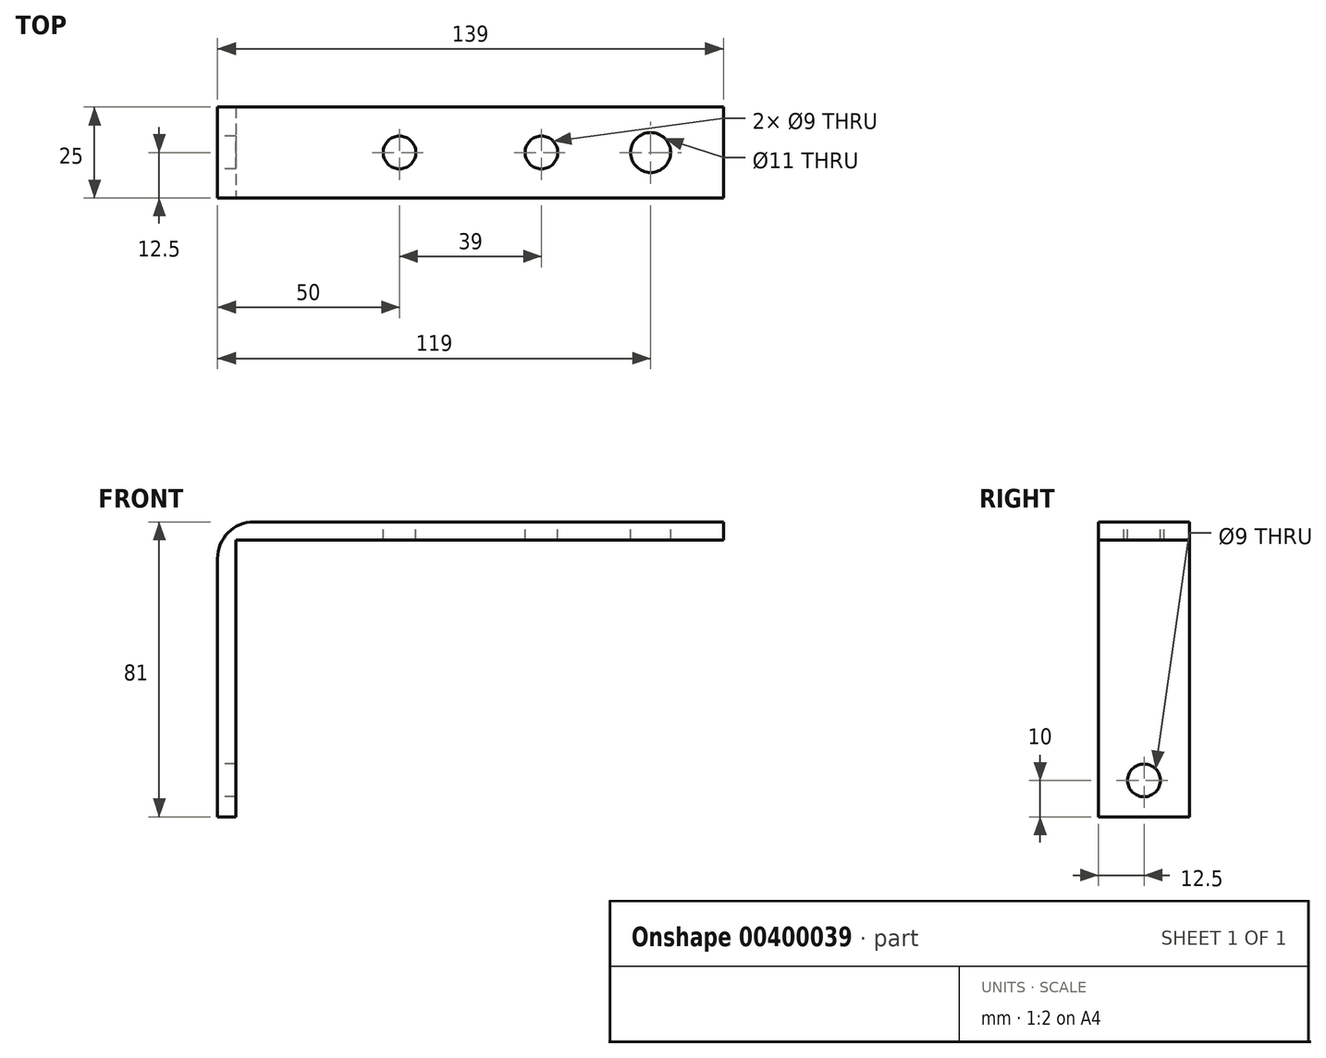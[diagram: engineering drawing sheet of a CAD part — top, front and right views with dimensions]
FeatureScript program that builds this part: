
annotation { "Feature Type Name" : "Feature", "Feature Type Description" : "" }
export const myFeature = defineFeature(function(context is Context, id is Id, definition is map)
    precondition{}
    {
        {
            var Q0;
            Q0=qCreatedBy(makeId("Front.planeOp"),FACE);
            var sketch = newSketch(context, id + "F0", { "sketchPlane" : qUnion([Q0])});
            skLineSegment(sketch, "E0.bottom", {"start": v(134, 5) * mm, "end": v(0, 5) * mm});
            skLineSegment(sketch, "E0.top", {"start": v(134, 0) * mm, "end": v(0, 0) * mm});
            skLineSegment(sketch, "E0.left", {"start": v(134, 5) * mm, "end": v(134, 0) * mm});
            skLineSegment(sketch, "E0.right", {"start": v(0, 5) * mm, "end": v(0, 0) * mm});
            skLineSegment(sketch, "E1.bottom", {"start": v(0, 5) * mm, "end": v(-5, 5) * mm});
            skLineSegment(sketch, "E1.top", {"start": v(0, -76) * mm, "end": v(-5, -76) * mm});
            skLineSegment(sketch, "E1.left", {"start": v(0, 5) * mm, "end": v(0, -76) * mm});
            skLineSegment(sketch, "E1.right", {"start": v(-5, 5) * mm, "end": v(-5, -76) * mm});
            skLineSegment(sketch, "E2", {"start": v(0, 0) * mm, "end": v(5, 0) * mm});
            skArc(sketch, "E3", {"start": v(5, 0) * mm, "mid": v(1.46, -1.46) * mm, "end": v(0, -5) * mm});
            skArc(sketch, "E4.0", {"start": v(5, 5) * mm, "mid": v(-2.07, 2.07) * mm, "end": v(-5, -5) * mm});
            skSolve(sketch);
        }
        {
            var Q0;
            Q0=makeQuery(id+"F0.imprint","IMPRINT",FACE,{"disambiguationData":[TD([[makeQuery(id+"F0.imprint","IMPRINT",EDGE,{"derivedFrom":sQuery(id+"F0.wireOp",EDGE,"E0.top")}),-1.0]])]});
            var Q1;
            {var subQ1=sQuery(id+"F0.wireOp",EDGE,"E1.top");Q1=makeQuery(id+"F0.imprint","IMPRINT",FACE,{"disambiguationData":[TD([[makeQuery(id+"F0.imprint","IMPRINT",EDGE,{"derivedFrom":subQ1}),-1.0]])]});}
            var Q2;
            {var subQ0=sQuery(id+"F0.wireOp",EDGE,"E2");Q2=makeQuery(id+"F0.imprint","IMPRINT",FACE,{"disambiguationData":[TD([[makeQuery(id+"F0.imprint","IMPRINT",EDGE,{"derivedFrom":subQ0}),-1.0]])]});}
            extrude(context, id + "F1", {"entities" : qUnion([Q0, Q1, Q2]), "oppositeDirection" : true, "depth" : 25 * mm});
        }
        {
            var Q0;
            Q0=makeQuery(id+"F1.opExtrude","SWEPT_FACE",FACE,{"disambiguationData":[OSD([sQuery(id+"F0.wireOp",EDGE,"E0.bottom")])]});
            var sketch = newSketch(context, id + "F2", { "sketchPlane" : qUnion([Q0])});
            skCircle(sketch, "E5", {"center": v(114, 12.5) * mm, "radius": 5.5 * mm});
            skCircle(sketch, "E6", {"center": v(84, 12.5) * mm, "radius": 4.5 * mm});
            skCircle(sketch, "E7", {"center": v(45, 12.5) * mm, "radius": 4.5 * mm});
            skSolve(sketch);
        }
        {
            var Q0;
            Q0=qSketchRegion(id+"F2",true);
            extrude(context, id + "F3", {"entities" : qUnion([Q0]), "operationType" : NewBodyOperationType.REMOVE, "oppositeDirection" : true, "depth" : 5 * mm});
        }
        {
            var Q0;
            Q0=qSketchRegion(id+"F2",true);
            extrude(context, id + "F4", {"entities" : qUnion([Q0]), "operationType" : NewBodyOperationType.REMOVE, "oppositeDirection" : true, "depth" : 5 * mm});
        }
        {
            var Q0;
            Q0=makeQuery(id+"F1.opExtrude","SWEPT_FACE",FACE,{"disambiguationData":[OSD([sQuery(id+"F0.wireOp",EDGE,"E1.right")])]});
            var sketch = newSketch(context, id + "F5", { "sketchPlane" : qUnion([Q0])});
            skCircle(sketch, "E8", {"center": v(-12.5, -66) * mm, "radius": 4.5 * mm});
            skSolve(sketch);
        }
        {
            var Q0;
            Q0=qSketchRegion(id+"F5",true);
            extrude(context, id + "F6", {"entities" : qUnion([Q0]), "operationType" : NewBodyOperationType.REMOVE, "oppositeDirection" : true, "depth" : 5 * mm});
        }
    });
